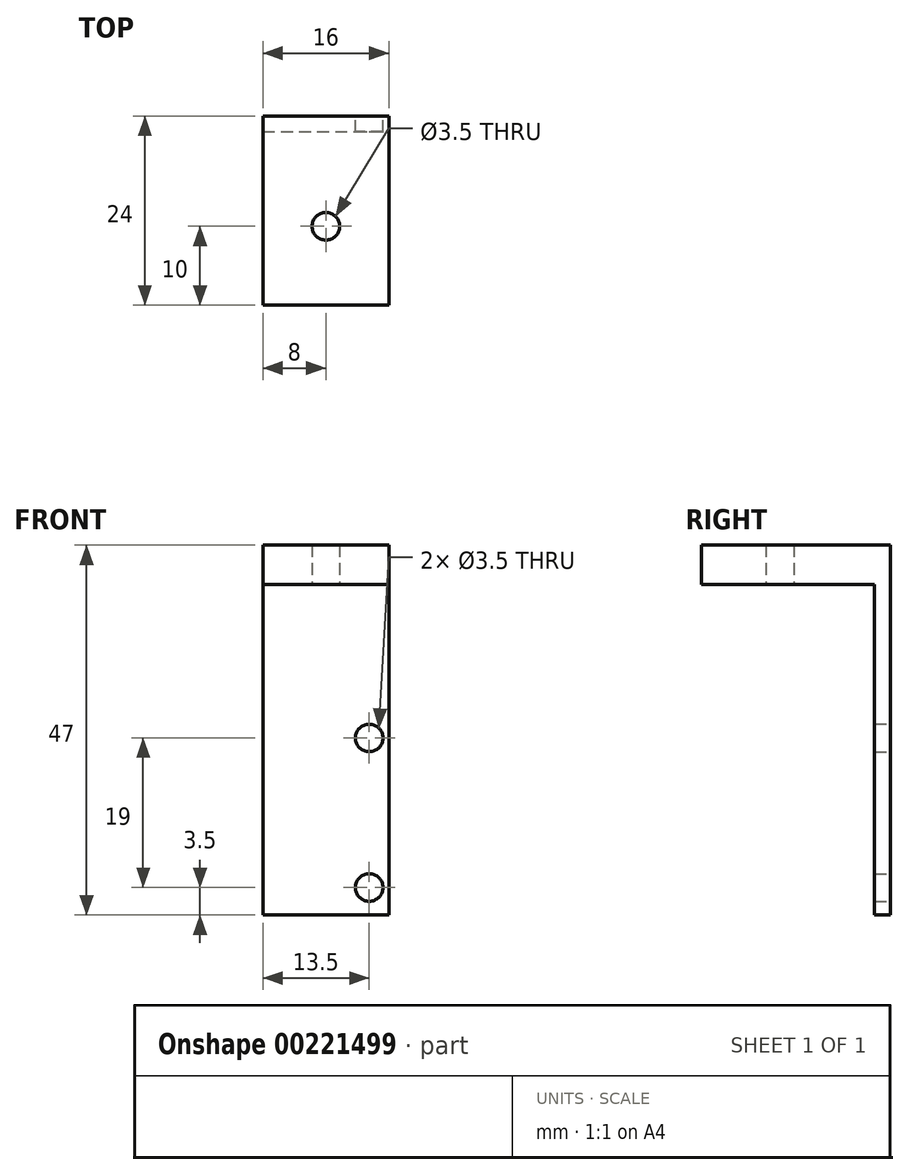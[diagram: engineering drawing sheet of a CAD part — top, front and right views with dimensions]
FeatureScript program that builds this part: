
annotation { "Feature Type Name" : "Feature", "Feature Type Description" : "" }
export const myFeature = defineFeature(function(context is Context, id is Id, definition is map)
    precondition{}
    {
        {
            var Q0;
            Q0=qCreatedBy(makeId("Front.planeOp"),FACE);
            var sketch = newSketch(context, id + "F0", { "sketchPlane" : qUnion([Q0])});
            skLineSegment(sketch, "E0.bottom", {"start": v(0, 0) * mm, "end": v(16, 0) * mm});
            skLineSegment(sketch, "E0.top", {"start": v(0, 42) * mm, "end": v(16, 42) * mm});
            skLineSegment(sketch, "E0.left", {"start": v(0, 0) * mm, "end": v(0, 42) * mm});
            skLineSegment(sketch, "E0.right", {"start": v(16, 0) * mm, "end": v(16, 42) * mm});
            skCircle(sketch, "E1", {"center": v(13.5, 3.5) * mm, "radius": 1.75 * mm});
            skCircle(sketch, "E2", {"center": v(13.5, 22.5) * mm, "radius": 1.75 * mm});
            skSolve(sketch);
        }
        {
            var Q0;
            Q0=makeQuery(id+"F0.imprint","IMPRINT",FACE,{"disambiguationData":[TD([[makeQuery(id+"F0.imprint","IMPRINT",EDGE,{"derivedFrom":sQuery(id+"F0.wireOp",EDGE,"E0.bottom")}),1.0]])]});
            extrude(context, id + "F1", {"entities" : qUnion([Q0]), "depth" : 2 * mm});
        }
        {
            var Q0;
            Q0=makeQuery(id+"F1.opExtrude","CAP_FACE",FACE,{"disambiguationData":[OSD([sQuery(id+"F0.wireOp",EDGE,"E0.bottom"),sQuery(id+"F0.wireOp",EDGE,"E0.top"),sQuery(id+"F0.wireOp",EDGE,"E0.left"),sQuery(id+"F0.wireOp",EDGE,"E0.right"),sQuery(id+"F0.wireOp",EDGE,"E1"),sQuery(id+"F0.wireOp",EDGE,"E2")])],"isStart":true});
            var sketch = newSketch(context, id + "F2", { "sketchPlane" : qUnion([Q0])});
            skLineSegment(sketch, "E3.bottom", {"start": v(0, 42) * mm, "end": v(-16, 42) * mm});
            skLineSegment(sketch, "E3.top", {"start": v(0, 47) * mm, "end": v(-16, 47) * mm});
            skLineSegment(sketch, "E3.left", {"start": v(0, 42) * mm, "end": v(0, 47) * mm});
            skLineSegment(sketch, "E3.right", {"start": v(-16, 42) * mm, "end": v(-16, 47) * mm});
            skSolve(sketch);
        }
        {
            var Q0;
            Q0=makeQuery(id+"F2.imprint","IMPRINT",FACE,{"disambiguationData":[TD([[makeQuery(id+"F2.imprint","IMPRINT",EDGE,{"derivedFrom":sQuery(id+"F2.wireOp",EDGE,"E3.bottom")}),-1.0]])]});
            extrude(context, id + "F3", {"entities" : qUnion([Q0]), "operationType" : NewBodyOperationType.ADD, "oppositeDirection" : true, "depth" : 24 * mm});
        }
        {
            var Q0;
            Q0=makeQuery(id+"F3.opExtrude","SWEPT_FACE",FACE,{"disambiguationData":[OSD([sQuery(id+"F2.wireOp",EDGE,"E3.bottom")])]});
            var sketch = newSketch(context, id + "F4", { "sketchPlane" : qUnion([Q0])});
            skCircle(sketch, "E4", {"center": v(8, 14) * mm, "radius": 1.75 * mm});
            skPoint(sketch, "E4.centerSnap0", {"position": v(8, 24) * mm});
            skSolve(sketch);
        }
        {
            var Q0;
            Q0=makeQuery(id+"F4.imprint","IMPRINT",FACE,{"disambiguationData":[TD([[makeQuery(id+"F4.imprint","IMPRINT",EDGE,{"derivedFrom":sQuery(id+"F4.wireOp",EDGE,"E4")}),1.0]])]});
            var Q1;
            Q1=makeQuery(id+"F3.opExtrude","SWEPT_FACE",FACE,{"disambiguationData":[OSD([sQuery(id+"F2.wireOp",EDGE,"E3.top")])]});
            extrude(context, id + "F5", {"entities" : qUnion([Q0]), "operationType" : NewBodyOperationType.REMOVE, "endBound" : BoundingType.UP_TO_SURFACE, "oppositeDirection" : true, "endBoundEntityFace" : qUnion([Q1]), "depth" : 25 * mm});
        }
    });
